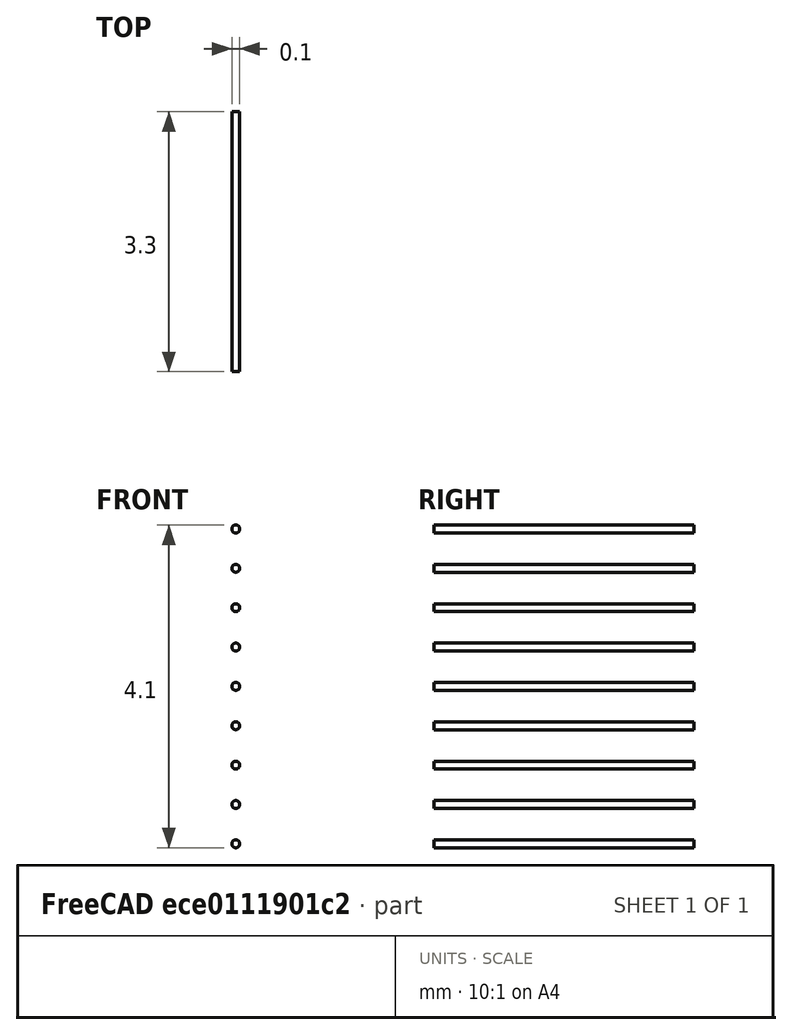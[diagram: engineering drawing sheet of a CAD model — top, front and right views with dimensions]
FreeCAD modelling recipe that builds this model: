
FCSTD DOCUMENT  (FreeCAD 0.16R6712 (Git))
Label: pins
License: All rights reserved
LicenseURL: http://en.wikipedia.org/wiki/All_rights_reserved
objects: Sketcher::SketchObject×1, PartDesign::Pad×1, Mesh::Feature×1
note: 3 computed .brp shape members not serialized (recipe doc carries the construction recipe); baked Part::Feature solids carry a one-line shape summary decoded from their .brp

FEATURE [Sketcher::SketchObject] Sketch
  Placement = pos=(0,0,0) rot=(1,0,0;1.5708rad)
  sketch-geometry (17):
    g0: Circle CenterX=0 CenterY=0 CenterZ=0 NormalX=0 NormalY=0 NormalZ=1 Radius=0.05
    g1: Circle CenterX=0 CenterY=0.5 CenterZ=0 NormalX=0 NormalY=0 NormalZ=1 Radius=0.05
    g2: LineSegment [constr] StartX=0 StartY=0 StartZ=0 EndX=0 EndY=0.5 EndZ=0
    g3: Circle CenterX=0 CenterY=1 CenterZ=0 NormalX=0 NormalY=0 NormalZ=1 Radius=0.05
    g4: LineSegment [constr] StartX=0 StartY=0.5 StartZ=0 EndX=0 EndY=1 EndZ=0
    g5: Circle CenterX=0 CenterY=1.5 CenterZ=0 NormalX=0 NormalY=0 NormalZ=1 Radius=0.05
    g6: LineSegment [constr] StartX=0 StartY=1 StartZ=0 EndX=0 EndY=1.5 EndZ=0
    g7: Circle CenterX=0 CenterY=2 CenterZ=0 NormalX=0 NormalY=0 NormalZ=1 Radius=0.05
    g8: LineSegment [constr] StartX=0 StartY=1.5 StartZ=0 EndX=0 EndY=2 EndZ=0
    g9: Circle CenterX=0 CenterY=-0.5 CenterZ=0 NormalX=0 NormalY=0 NormalZ=1 Radius=0.05
    g10: LineSegment [constr] StartX=0 StartY=0 StartZ=0 EndX=0 EndY=-0.5 EndZ=0
    g11: Circle CenterX=0 CenterY=-1 CenterZ=0 NormalX=0 NormalY=0 NormalZ=1 Radius=0.05
    g12: LineSegment [constr] StartX=0 StartY=-0.5 StartZ=0 EndX=0 EndY=-1 EndZ=0
    g13: Circle CenterX=0 CenterY=-1.5 CenterZ=0 NormalX=0 NormalY=0 NormalZ=1 Radius=0.05
    g14: LineSegment [constr] StartX=0 StartY=-1 StartZ=0 EndX=0 EndY=-1.5 EndZ=0
    g15: Circle CenterX=0 CenterY=-2 CenterZ=0 NormalX=0 NormalY=0 NormalZ=1 Radius=0.05
    g16: LineSegment [constr] StartX=0 StartY=-1.5 StartZ=0 EndX=0 EndY=-2 EndZ=0
  constraints (42):
    c: Radius(g0) = 0.05
    c: Coincident(g0,g-1)
    c: Radius(g1) = 0.05
    c: Coincident(g0,g2)
    c: Coincident(g1,g2)
    c: Distance(g2) = 0.5
    c: Angle(g2) = 1.5708
    c: Radius(g3) = 0.05
    c: Coincident(g1,g4)
    c: Coincident(g3,g4)
    c: Equal(g2,g4)
    c: Parallel(g4,g2)
    c: Radius(g5) = 0.05
    c: Coincident(g3,g6)
    c: Coincident(g5,g6)
    c: Equal(g2,g6)
    c: Parallel(g6,g2)
    c: Radius(g7) = 0.05
    c: Coincident(g5,g8)
    c: Coincident(g7,g8)
    c: Equal(g2,g8)
    c: Parallel(g8,g2)
    c: Radius(g9) = 0.05
    c: Coincident(g0,g10)
    c: Coincident(g9,g10)
    c: Distance(g10) = 0.5
    c: Angle(g10) = -1.5708
    c: Radius(g11) = 0.05
    c: Coincident(g9,g12)
    c: Coincident(g11,g12)
    c: Equal(g10,g12)
    c: Parallel(g12,g10)
    c: Radius(g13) = 0.05
    c: Coincident(g11,g14)
    c: Coincident(g13,g14)
    c: Equal(g10,g14)
    c: Parallel(g14,g10)
    c: Radius(g15) = 0.05
    c: Coincident(g13,g16)
    c: Coincident(g15,g16)
    c: Equal(g10,g16)
    c: Parallel(g16,g10)
FEATURE [PartDesign::Pad] Pad
  Length = 3
  Length2 = 0.3
  Placement = pos=(0,0,0) rot=(1,0,0;1.5708rad)
  Sketch = -> Sketch
  Type = 4
FEATURE [Mesh::Feature] Mesh  label="Pad (Meshed)"
